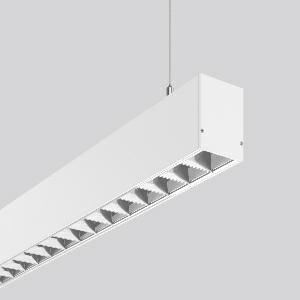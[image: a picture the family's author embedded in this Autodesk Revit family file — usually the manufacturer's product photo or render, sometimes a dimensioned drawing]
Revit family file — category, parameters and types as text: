
# Revit family: less_is_more_50_312343_002_76_5d40
name_source: partatom
category: Lighting Fixtures
units: mm (PartAtom-declared; Revit-internal decimal feet)

## family parameters
Cut with Voids When Loaded = No
Host = Face
Light Source = No
Part Type = Normal
Room Calculation Point = No
Round Connector Dimension = Use Diameter
Shared = No

## types (1)
- LESS IS MORE 50 (1 x LED Modul 830, 6400 lm, 3000)
    Apparent Load = 58 VA
    CIE Flux Codes = 95 100 100 63 100
    Color Rendering = 80
    Color Temperature = 3000
    Default Elevation = 1800 mm
    Description = Series: LESS IS MORE 50
Linear pendant luminaire for aesthetically sophisticated lighting. Housing: extruded aluminium profile, powder-coated. End cap aluminium powder-coated. Canopy made of aluminium, powder-coated. Alea optical system: Reflector structure (ABS, Aluminium-coated, highly polished) with integrated diffuser made of non-yellowing plastic (PMMA) opal for glare-free light at the workstation (screen-compliant according to EN 12464-1). Direct 65%, indirect 35% light emission. Controlled separately. Suitable for pendant. 2-point steel cable suspension freely positionable and infinitely height-adjustable. Special lengths available on request. LED unit with integrated converter interchangeable and removable. Suitable for through-wiring. With sensors or as a safety luminaire on request. 
Colour: traffic white, matt (RAL 9016)
Length: 1407 mm
Width: 57 mm
Height: 75 mm
Suspension length: 2000 mm
Lamp: LED
Socket: without socket
Colour temperature: 3000K
Colour rendering index (CRI): 80
Light source: LED
Socket lamp2: Without base
Colour temperature: 3000K
System power: 58 W
Rated luminous flux: 6400 lm
Luminous efficiency: 110 lm/W
Control gear: Converter, dimmable, DALI
Control gear: Converter, dimmable, DALI
Protection class: I
Type of protection: IP 20
    Height = 75 mm
    Lamp = 1 x LED Modul 830
    Lamp Light Flux = 6400 lm
    Lamp count = 1
    Length = 1407 mm
    Lifetime = 50000 h
    Luminous efficacy = 110 lm/W
    Manufacturer = RZB
    ModVariant = No
    Model = 312343.002.76
    Mounting Place = Ceiling
    Mounting Type = Pendant
    Number of Poles = 1
    OnlyDefault = Yes
    Power Factor = 1
    Product Name = LESS IS MORE 50
    Product group = Pendant LED linear luminaires
    ProductGroupID = 907
    Protection Class = Protection class I
    Protection Degree = IP 20
    RLX_Detail_Level = 1
    RLX_Emergency_Light_Flux = 0 lm
    RLX_Emergency_Type = 0
    RLX_Emergency_Type_DB = No
    RlxData = <blob elided: 37465 chars, md5=cbac6d89>
    Socket = socket
    Standby Power = 0 W
    System Light Flux = 6400 lm
    System Power = 58 W
    Type Comments = Product without accessories
    Type Image = 312342.002.jpg
    URL = http://relux.com
    VarID = ---
    Voltage = 230 V
    Voltage Range = 220-240 V
    Weight = 0.00 kg
    Width = 57 mm

## geometry (parser evidence)
native form markers: Blend x4, Sweep x13
no freeform markers — native parametric forms only
